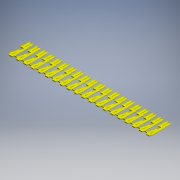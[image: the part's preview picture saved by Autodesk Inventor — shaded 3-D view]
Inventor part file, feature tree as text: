
AUTODESK INVENTOR PART (.ipt)
format: ipt  version: 2017.3 (Build 213256000, 256)  size: 680,448 bytes
history: native  units: mm (DEFAULTED — no unit token found)
features: other x14, extrude x2, sketch x2, pattern_linear x1
ambient origin geometry x8: Origin, YZ Plane, XZ Plane, XY Plane, X Axis, Y Axis, Z Axis, Center Point
bodies: Solid1 (feature_tree)
feature tree (19):
  extrude  "Extrusion1"  Depth=0.6604mm TaperAngle=0.0deg
  extrude  "Extrusion2"  [1 undecoded]
  pattern_linear  "Rectangular Pattern1"  [2 undecoded]
  other  "pin_XY"
  other  "pin_YZ"
  other  "pin_ZX"
  other  "pin_X"
  other  "pin_Y"
  other  "pin_Z"
  other  "pin_Center"
  other  "pin_reverse_XY"
  other  "pin_reverse_YZ"
  other  "pin_reverse_ZX"
  other  "pin_reverse_X"
  other  "pin_reverse_Y"
  other  "pin_reverse_Z"
  other  "pin_reverse_Center"
  sketch  "Sketch_4"  dims[d4=200.0mm d6=2.54mm d7=10.0mm d9=0.0mm]
  sketch  "Sketch_2"  dims[d0=0.3302mm d1=0.0mm d2=0.6604mm d3=0.0mm]
note: 3 required parameter values undecoded (feature->parameter linkage not recoverable at this tier; creation-order binding heuristic only, values carry confidence <= 0.55)
